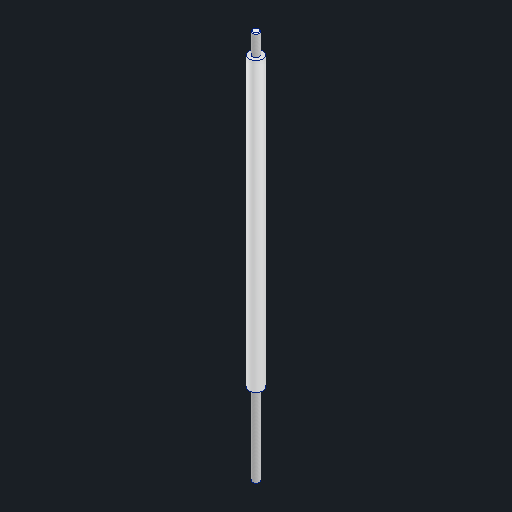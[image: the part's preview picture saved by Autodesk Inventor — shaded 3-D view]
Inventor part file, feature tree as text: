
AUTODESK INVENTOR PART (.ipt)
format: ipt  version: 2025.3 (Build 293356030, 356C)  size: 259,072 bytes
history: native  units: mm
features: other x1, revolve x1, thread x1, chamfer x1, sketch x1
ambient origin geometry x8: Origin, YZ Plane, XZ Plane, XY Plane, X Axis, Y Axis, Z Axis, Center Point
bodies: Body1 (feature_tree)
feature tree (5):
  other  "Sólido1"
  revolve  "Revolución1"  [1 undecoded]
  thread  "Rosca1"  [1 undecoded]
  chamfer  "Chaflán1"  Distance=123.0mm
  sketch  "Boceto1"  dims[d1=3.0mm d2=6.0mm d3=9.0mm d4=123.0mm d5=90.0deg d6=144.0mm d7=0.0mm d8=35.0mm d9=0.306725mm d10=2.0mm d11=45.0deg]
note: 2 required parameter values undecoded (feature->parameter linkage not recoverable at this tier; creation-order binding heuristic only, values carry confidence <= 0.55)